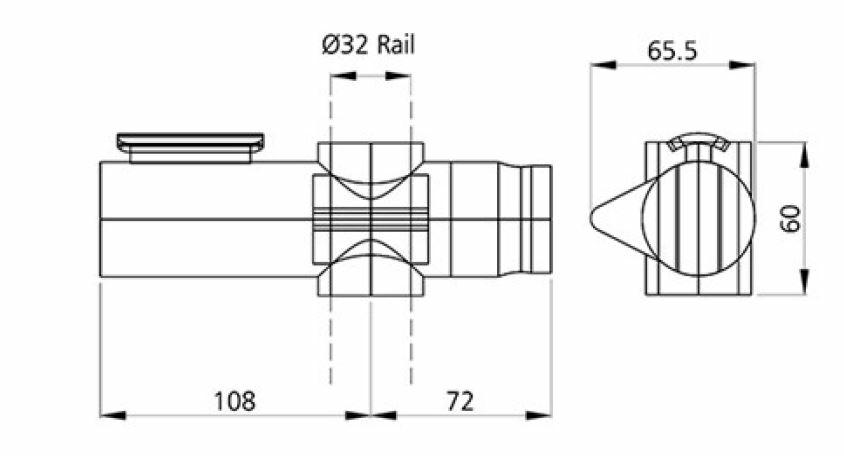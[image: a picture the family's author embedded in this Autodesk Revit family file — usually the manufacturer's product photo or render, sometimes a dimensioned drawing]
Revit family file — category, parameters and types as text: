
# Revit family: RBA4801-722
name_source: partatom
category: Plumbing Fixtures
units: mm (PartAtom-declared; Revit-internal decimal feet)

## family parameters
Always vertical = Yes
Cut with Voids When Loaded = No
Part Type = Normal
Room Calculation Point = No
Round Connector Dimension = Use Diameter
Shared = Yes
Work Plane-Based = No

## types (1)
- RBA4801-722
    CW Connection = Yes
    Default Elevation = 0 mm  [stored 0 ft]
    Description = Modular Shower T-Rail & Mixer Kit, Satin
    Distance Away from Toilet (default) = 1090 mm  [stored 3.57612 ft]
    Distance Away from Wall (default) = 100 mm  [stored 0.328084 ft]
    HW Connection = Yes
    Manufacturer = RBA Group
    Materials and Finishes = Stainless Steel Satin Finish
    Model = RBA4801-722
    OFFSET = 1000 mm  [stored 3.28084 ft]
    URL = www.rba.com.au
    Vent Connection = Yes
    Waste Connection = Yes

note: [stored X ft] marks values corroborated as IEEE doubles in the binary element streams (Revit-internal decimal feet)

## geometry (parser evidence)
native form markers: Blend x4, Sweep x13
no freeform markers — native parametric forms only
